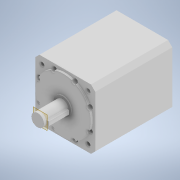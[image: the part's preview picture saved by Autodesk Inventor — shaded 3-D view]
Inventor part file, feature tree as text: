
AUTODESK INVENTOR PART (.ipt)
format: ipt  version: 2022 (Build 260153000, 153)  size: 229,888 bytes
history: native  units: in
note: dims shown in document units (in); Inventor stores cm internally (conversion verified against a paired STEP export)
features: extrude x10, sketch x10, plane x1, chamfer x1
ambient origin geometry x8: Origin, YZ Plane, XZ Plane, XY Plane, X Axis, Y Axis, Z Axis, Center Point
bodies: Solid1 (feature_tree)
feature tree (22):
  extrude  "Extrusion1"  Depth=4.7244in
  extrude  "Extrusion2"  Depth=4.3307in
  extrude  "Extrusion3"  Depth=0.1575in
  extrude  "Extrusion4"  Depth=0.0787in
  extrude  "Extrusion5"  Depth=1.9291in
  extrude  "Extrusion6"  Depth=1.5748in TaperAngle=360.0deg
  plane  "Work Plane1"
  extrude  "Extrusion7"  Depth=1.9685in
  extrude  "Extrusion8"  Depth=4.3307in
  extrude  "Extrusion9"  Depth=1.9685in TaperAngle=0.0deg
  extrude  "Extrusion10"  Depth=0.315in
  chamfer  "Chamfer1"  Distance=0.315in
  sketch  "Sketch1"  dims[d0=4.7244in d1=4.7244in]
  sketch  "Sketch2"  dims[d2=6.063in d3=0.0in d4=4.3307in]
  sketch  "Sketch3"  dims[d5=0.1575in d6=0.0in d7=1.378in]
  sketch  "Sketch4"  dims[d8=0.0787in d9=0.0in d10=0.9843in]
  sketch  "Sketch5"  dims[d11=1.9291in d12=0.0in d13=0.3346in]
  sketch  "Sketch6"  dims[d14=5.1181in d15=1.5748in d17=360.0deg]
  sketch  "Sketch7"  dims[d19=1.9685in d20=0.0in d21=0.3346in]
  sketch  "Sketch8"  dims[d22=22.5deg d23=4.3307in]
  sketch  "Sketch9"  dims[d24=3.1496in d26=360.0deg d28=1.9685in d29=0.0in]
  sketch  "Sketch10"  dims[d30=-0.1969in d31=0.315in d32=0.315in d33=1.5748in d34=0.0in d35=0.748in d36=1.5748in d37=0.0in d38=3.7402in d39=0.1181in d40=0.0in d41=4.9213in d42=0.374in d43=1.5748in d45=360.0deg d47=1.9685in d48=0.0in d49=0.3346in d50=0.0787in d51=45.0deg]
